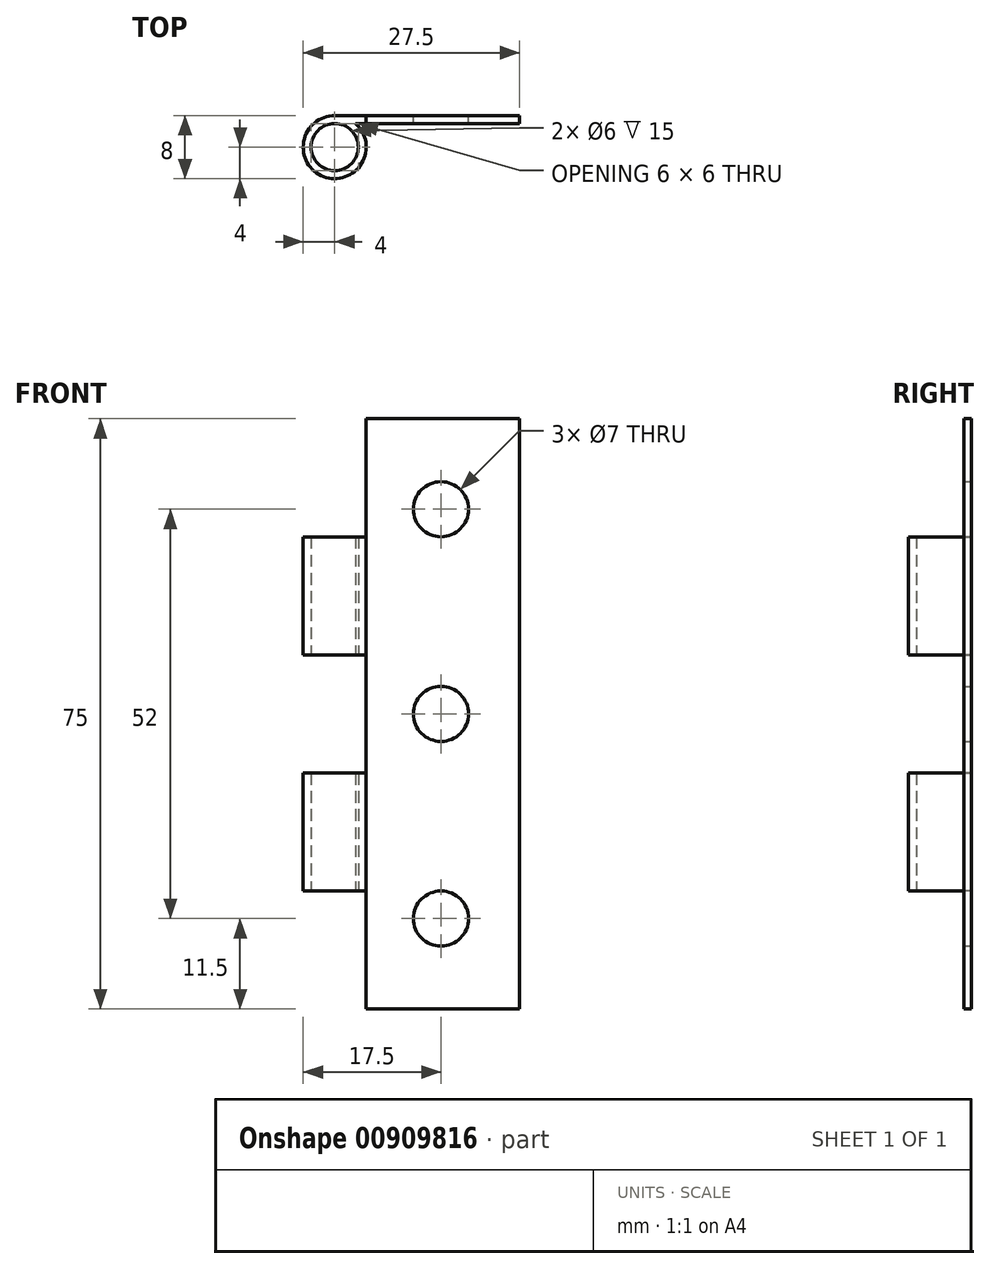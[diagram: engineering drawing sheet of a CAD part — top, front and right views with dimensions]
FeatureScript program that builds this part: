
annotation { "Feature Type Name" : "Feature", "Feature Type Description" : "" }
export const myFeature = defineFeature(function(context is Context, id is Id, definition is map)
    precondition{}
    {
        {
            var Q0;
            Q0=qCreatedBy(makeId("Front.planeOp"),FACE);
            var sketch = newSketch(context, id + "F0", { "sketchPlane" : qUnion([Q0])});
            skLineSegment(sketch, "E0.bottom", {"start": v(0, 37.5) * mm, "end": v(-20, 37.5) * mm});
            skLineSegment(sketch, "E0.top", {"start": v(0, -37.5) * mm, "end": v(-20, -37.5) * mm});
            skLineSegment(sketch, "E0.left", {"start": v(0, 37.5) * mm, "end": v(0, -37.5) * mm});
            skLineSegment(sketch, "E0.right", {"start": v(-20, 37.5) * mm, "end": v(-20, -37.5) * mm});
            skCircle(sketch, "E1", {"center": v(-10, 26) * mm, "radius": 3.5 * mm});
            skCircle(sketch, "E2", {"center": v(-10, 0) * mm, "radius": 3.5 * mm});
            skCircle(sketch, "E3", {"center": v(-10, -26) * mm, "radius": 3.5 * mm});
            skSolve(sketch);
        }
        {
            var Q0;
            Q0=makeQuery(id+"F0.imprint","IMPRINT",FACE,{"disambiguationData":[TD([[makeQuery(id+"F0.imprint","IMPRINT",EDGE,{"derivedFrom":sQuery(id+"F0.wireOp",EDGE,"E0.bottom")}),1.0]])]});
            extrude(context, id + "F1", {"entities" : qUnion([Q0]), "depth" : 1 * mm, "offsetDistance" : 25 * mm});
        }
        {
            var Q0;
            Q0=makeQuery(id+"F1.opExtrude","SWEPT_FACE",FACE,{"disambiguationData":[OSD([sQuery(id+"F0.wireOp",EDGE,"E0.top")])]});
            var sketch = newSketch(context, id + "F2", { "sketchPlane" : qUnion([Q0])});
            skCircle(sketch, "E4", {"center": v(-23.5, 4) * mm, "radius": 4 * mm});
            skLineSegment(sketch, "E5", {"start": v(-20, 0) * mm, "end": v(-23.5, 0) * mm});
            skLineSegment(sketch, "E6", {"start": v(-20, 1) * mm, "end": v(-20.85, 1) * mm});
            skCircle(sketch, "E7", {"center": v(-23.5, 4) * mm, "radius": 3 * mm});
            skSolve(sketch);
        }
        {
            var Q0;
            Q0=qSketchRegion(id+"F2",true);
            var Q1;
            {var subQ0=sQuery(id+"F2.wireOp",EDGE,"E5");Q1=makeQuery(id+"F2.imprint","IMPRINT",FACE,{"disambiguationData":[TD([[makeQuery(id+"F2.imprint","IMPRINT",EDGE,{"derivedFrom":subQ0}),-1.0]])]});}
            var Q2;
            Q2=makeQuery(id+"F1.opExtrude","SWEPT_FACE",FACE,{"disambiguationData":[OSD([sQuery(id+"F0.wireOp",EDGE,"E0.bottom")])]});
            extrude(context, id + "F3", {"entities" : qUnion([Q0, Q1]), "operationType" : NewBodyOperationType.ADD, "endBound" : BoundingType.UP_TO_SURFACE, "oppositeDirection" : true, "depth" : 25 * mm, "endBoundEntityFace" : qUnion([Q2]), "offsetDistance" : 25 * mm});
        }
        {
            var Q0;
            Q0=makeQuery(id+"F3.boolean.opBoolean","MERGE",FACE,{"derivedFrom":[makeQuery(id+"F1.opExtrude","CAP_FACE",FACE,{"disambiguationData":[OSD([sQuery(id+"F0.wireOp",EDGE,"E0.bottom"),sQuery(id+"F0.wireOp",EDGE,"E0.top"),sQuery(id+"F0.wireOp",EDGE,"E0.left"),sQuery(id+"F0.wireOp",EDGE,"E0.right"),sQuery(id+"F0.wireOp",EDGE,"E1"),sQuery(id+"F0.wireOp",EDGE,"E2"),sQuery(id+"F0.wireOp",EDGE,"E3")])],"isStart":false}),makeQuery(id+"F3.opExtrude","SWEPT_FACE",FACE,{"disambiguationData":[OSD([sQuery(id+"F2.wireOp",EDGE,"E6")])]})]});
            var sketch = newSketch(context, id + "F4", { "sketchPlane" : qUnion([Q0])});
            skLineSegment(sketch, "E8.bottom", {"start": v(-19.5, 37.5) * mm, "end": v(-27.5, 37.5) * mm});
            skLineSegment(sketch, "E8.top", {"start": v(-19.5, 22.5) * mm, "end": v(-27.5, 22.5) * mm});
            skLineSegment(sketch, "E8.left", {"start": v(-19.5, 37.5) * mm, "end": v(-19.5, 22.5) * mm});
            skLineSegment(sketch, "E8.right", {"start": v(-27.5, 37.5) * mm, "end": v(-27.5, 22.5) * mm});
            skLineSegment(sketch, "E9.bottom", {"start": v(-27.5, 7.5) * mm, "end": v(-19.5, 7.5) * mm});
            skLineSegment(sketch, "E9.top", {"start": v(-27.5, -7.5) * mm, "end": v(-19.5, -7.5) * mm});
            skLineSegment(sketch, "E9.left", {"start": v(-27.5, 7.5) * mm, "end": v(-27.5, -7.5) * mm});
            skLineSegment(sketch, "E9.right", {"start": v(-19.5, 7.5) * mm, "end": v(-19.5, -7.5) * mm});
            skLineSegment(sketch, "E10.bottom", {"start": v(-19.5, -37.5) * mm, "end": v(-27.5, -37.5) * mm});
            skLineSegment(sketch, "E10.top", {"start": v(-19.5, -22.5) * mm, "end": v(-27.5, -22.5) * mm});
            skLineSegment(sketch, "E10.left", {"start": v(-19.5, -37.5) * mm, "end": v(-19.5, -22.5) * mm});
            skLineSegment(sketch, "E10.right", {"start": v(-27.5, -37.5) * mm, "end": v(-27.5, -22.5) * mm});
            skLineSegment(sketch, "E11", {"start": v(-19.5, 22.5) * mm, "end": v(-19.5, 7.5) * mm});
            skLineSegment(sketch, "E12", {"start": v(-19.5, -7.5) * mm, "end": v(-19.5, -22.5) * mm});
            skSolve(sketch);
        }
        {
            var Q0;
            Q0 = qSketchRegion(id + "F4", true);
            extrude(context, id + "F5", {"entities" : qUnion([Q0]), "operationType" : NewBodyOperationType.REMOVE, "endBound" : BoundingType.THROUGH_ALL, "oppositeDirection" : true, "depth" : 25 * mm, "offsetDistance" : 25 * mm, "hasSecondDirection" : true, "secondDirectionBound" : SecondDirectionBoundingType.THROUGH_ALL, "secondDirectionOppositeDirection" : false, "secondDirectionDepth" : 25 * mm});
        }
    });
